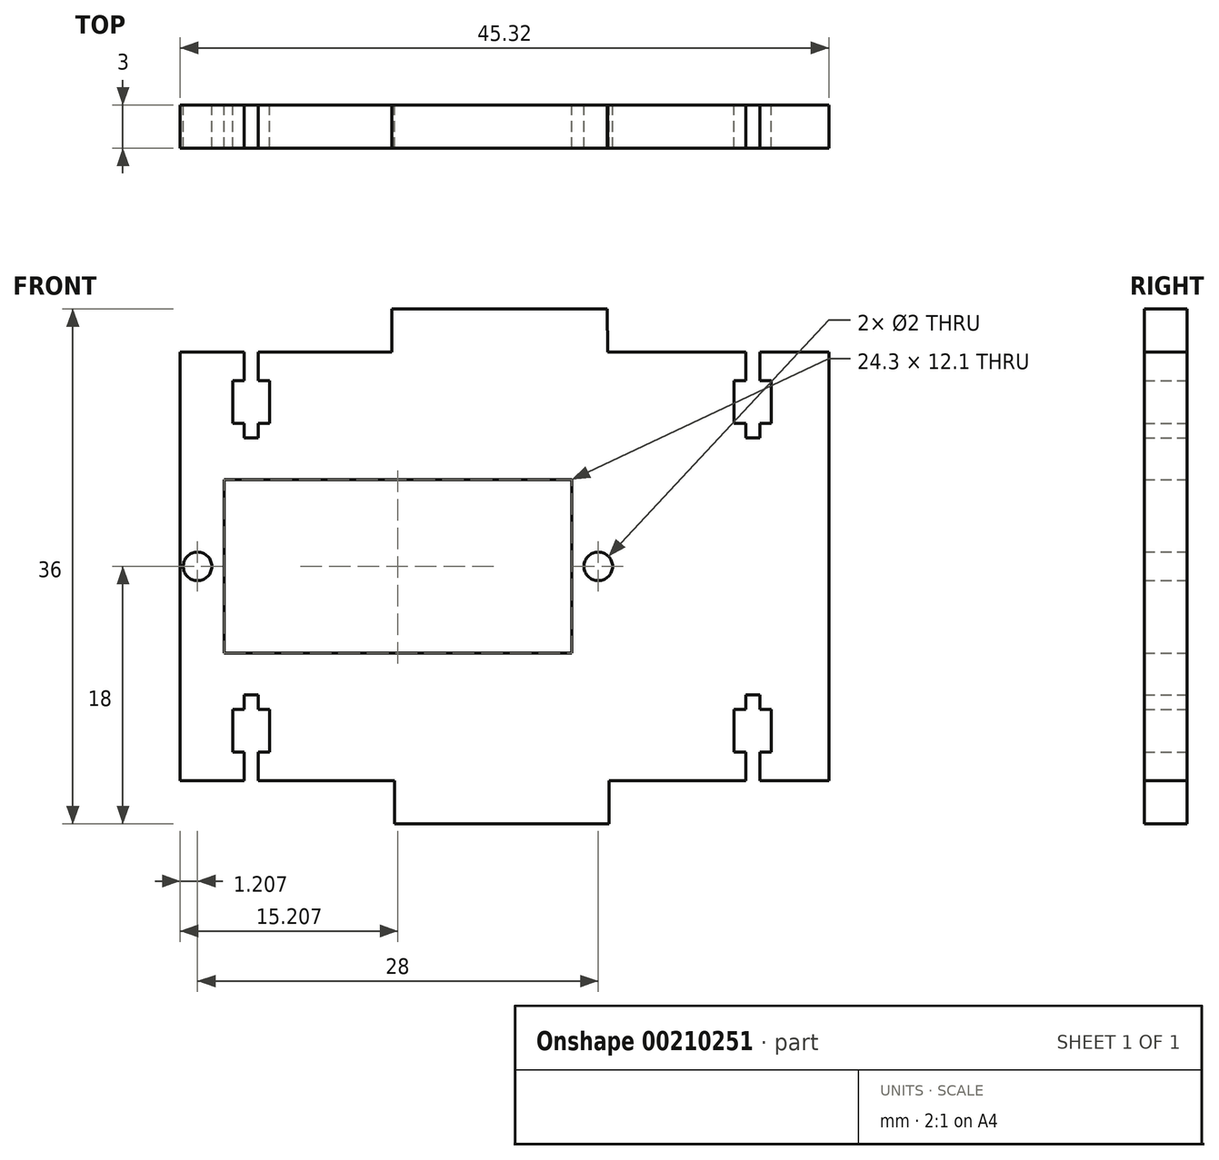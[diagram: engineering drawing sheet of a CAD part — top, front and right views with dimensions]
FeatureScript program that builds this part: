
annotation { "Feature Type Name" : "Feature", "Feature Type Description" : "" }
export const myFeature = defineFeature(function(context is Context, id is Id, definition is map)
    precondition{}
    {
        {
            var Q0;
            Q0=qCreatedBy(makeId("Top.planeOp"),FACE);
            var sketch = newSketch(context, id + "F0", { "sketchPlane" : qUnion([Q0])});
            skCircle(sketch, "E0", {"center": v(38.16, 0) * mm, "radius": 1.5 * mm});
            skArc(sketch, "E1", {"start": v(38.16, -5) * mm, "mid": v(43.16, 0) * mm, "end": v(38.16, 5) * mm});
            skLineSegment(sketch, "E2", {"start": v(38.16, 0) * mm, "end": v(36.66, 0) * mm});
            skLineSegment(sketch, "E3", {"start": v(-21.84, 0) * mm, "end": v(-21.84, 0) * mm});
            skLineSegment(sketch, "E4", {"start": v(-16.84, 5) * mm, "end": v(38.16, 5) * mm});
            skLineSegment(sketch, "E5.MirrorCS", {"start": v(-16.84, -5) * mm, "end": v(38.16, -5) * mm});
            skPoint(sketch, "E6", {"position": v(8.16, 0) * mm});
            skPoint(sketch, "E7", {"position": v(-6.84, 0) * mm});
            skPoint(sketch, "E8", {"position": v(-16.84, 0) * mm});
            skCircle(sketch, "E9", {"center": v(18.16, 0) * mm, "radius": 1.5 * mm});
            skCircle(sketch, "E10", {"center": v(-16.84, 0) * mm, "radius": 1.5 * mm});
            skLineSegment(sketch, "E11", {"start": v(-6.84, 0) * mm, "end": v(-6.84, 1.5) * mm});
            skLineSegment(sketch, "E12", {"start": v(-6.84, 1.5) * mm, "end": v(8.13, 1.5) * mm});
            skLineSegment(sketch, "E13", {"start": v(8.16, 0) * mm, "end": v(8.13, 1.5) * mm});
            skLineSegment(sketch, "E14.MirrorCS", {"start": v(8.16, 0) * mm, "end": v(8.13, -1.5) * mm});
            skLineSegment(sketch, "E15.MirrorCS", {"start": v(-6.84, -1.5) * mm, "end": v(8.13, -1.5) * mm});
            skLineSegment(sketch, "E16.MirrorCS", {"start": v(-6.84, 0) * mm, "end": v(-6.84, -1.5) * mm});
            skPoint(sketch, "E17.visualSharp", {"position": v(-21.84, 5) * mm});
            skArc(sketch, "E17.filletArc", {"start": v(-16.84, 5) * mm, "mid": v(-20.38, 3.54) * mm, "end": v(-21.84, 0) * mm});
            skPoint(sketch, "E18.visualSharp", {"position": v(-21.84, -5) * mm});
            skArc(sketch, "E18.filletArc", {"start": v(-21.84, 0) * mm, "mid": v(-20.38, -3.54) * mm, "end": v(-16.84, -5) * mm});
            skSolve(sketch);
        }
        {
            var Q0;
            Q0=qCreatedBy(makeId("Top.planeOp"),FACE);
            cPlane(context, id + "F1", {"entities" : qUnion([Q0]), "cplaneType" : CPlaneType.OFFSET, "offset" : 30 * mm, "width" : 150 * mm, "height" : 150 * mm});
        }
        {
            var Q0;
            Q0=qCreatedBy(id+"F1.planeOp",FACE);
            var sketch = newSketch(context, id + "F2", { "sketchPlane" : qUnion([Q0])});
            skCircle(sketch, "E19", {"center": v(38.16, 0) * mm, "radius": 2.45 * mm});
            skArc(sketch, "E20", {"start": v(38.16, -5) * mm, "mid": v(43.16, 0) * mm, "end": v(38.16, 5) * mm});
            skLineSegment(sketch, "E21", {"start": v(38.16, 0) * mm, "end": v(35.7, 0) * mm});
            skLineSegment(sketch, "E22", {"start": v(-21.84, 0) * mm, "end": v(-21.84, 0) * mm});
            skLineSegment(sketch, "E23", {"start": v(-16.84, 5) * mm, "end": v(38.16, 5) * mm});
            skLineSegment(sketch, "E24.MirrorCS", {"start": v(-16.84, -5) * mm, "end": v(38.16, -5) * mm});
            skPoint(sketch, "E25", {"position": v(8.16, 0) * mm});
            skPoint(sketch, "E26", {"position": v(-6.84, 0) * mm});
            skPoint(sketch, "E27", {"position": v(-16.84, 0) * mm});
            skCircle(sketch, "E28", {"center": v(18.16, 0) * mm, "radius": 1.5 * mm});
            skCircle(sketch, "E29", {"center": v(-16.84, 0) * mm, "radius": 1.5 * mm});
            skLineSegment(sketch, "E30", {"start": v(-6.84, 0) * mm, "end": v(-6.84, 1.5) * mm});
            skLineSegment(sketch, "E31", {"start": v(-6.84, 1.5) * mm, "end": v(8.13, 1.5) * mm});
            skLineSegment(sketch, "E32", {"start": v(8.16, 0) * mm, "end": v(8.13, 1.5) * mm});
            skLineSegment(sketch, "E33.MirrorCS", {"start": v(8.16, 0) * mm, "end": v(8.13, -1.5) * mm});
            skLineSegment(sketch, "E34.MirrorCS", {"start": v(-6.84, -1.5) * mm, "end": v(8.13, -1.5) * mm});
            skLineSegment(sketch, "E35.MirrorCS", {"start": v(-6.84, 0) * mm, "end": v(-6.84, -1.5) * mm});
            skPoint(sketch, "E36.visualSharp", {"position": v(-21.84, 5) * mm});
            skArc(sketch, "E36.filletArc", {"start": v(-16.84, 5) * mm, "mid": v(-20.38, 3.54) * mm, "end": v(-21.84, 0) * mm});
            skPoint(sketch, "E37.visualSharp", {"position": v(-21.84, -5) * mm});
            skArc(sketch, "E37.filletArc", {"start": v(-21.84, 0) * mm, "mid": v(-20.38, -3.54) * mm, "end": v(-16.84, -5) * mm});
            skSolve(sketch);
        }
        {
            var Q0;
            Q0=qCreatedBy(makeId("Front.planeOp"),FACE);
            var sketch = newSketch(context, id + "F3", { "sketchPlane" : qUnion([Q0])});
            skLineSegment(sketch, "E38", {"start": v(0, 30.19) * mm, "end": v(0, 30) * mm});
            skLineSegment(sketch, "E39.0", {"start": v(36.66, 0) * mm, "end": v(39.66, 0) * mm});
            skLineSegment(sketch, "E39.1", {"start": v(38.16, 0) * mm, "end": v(38.56, 0) * mm});
            skLineSegment(sketch, "E39.2", {"start": v(38.16, 0) * mm, "end": v(36.66, 0) * mm});
            skPoint(sketch, "E39.3", {"position": v(-21.84, 0) * mm});
            skLineSegment(sketch, "E39.4", {"start": v(-16.84, 0) * mm, "end": v(38.16, 0) * mm});
            skLineSegment(sketch, "E39.5", {"start": v(-16.84, 0) * mm, "end": v(-16.84, 0) * mm});
            skPoint(sketch, "E39.6", {"position": v(-21.84, 0) * mm});
            skPoint(sketch, "E39.7", {"position": v(8.16, 0) * mm});
            skPoint(sketch, "E39.8", {"position": v(-6.84, 0) * mm});
            skPoint(sketch, "E39.9", {"position": v(-16.84, 0) * mm});
            skLineSegment(sketch, "E39.10", {"start": v(16.66, 0) * mm, "end": v(19.66, 0) * mm});
            skLineSegment(sketch, "E39.11", {"start": v(-18.34, 0) * mm, "end": v(-17.34, 0) * mm});
            skLineSegment(sketch, "E39.14", {"start": v(8.16, 0) * mm, "end": v(8.13, 0) * mm});
            skLineSegment(sketch, "E39.15", {"start": v(8.16, 0) * mm, "end": v(8.13, 0) * mm});
            skLineSegment(sketch, "E39.16", {"start": v(-6.84, 0) * mm, "end": v(8.13, 0) * mm});
            skPoint(sketch, "E39.18", {"position": v(-21.84, 0) * mm});
            skLineSegment(sketch, "E39.19", {"start": v(-16.84, 0) * mm, "end": v(-21.84, 0) * mm});
            skPoint(sketch, "E39.20", {"position": v(-21.84, 0) * mm});
            skLineSegment(sketch, "E39.21", {"start": v(-21.84, 0) * mm, "end": v(-16.84, 0) * mm});
            skLineSegment(sketch, "E39.22.0", {"start": v(-17.34, 30) * mm, "end": v(-21.84, 30) * mm});
            skLineSegment(sketch, "E39.22.1", {"start": v(-21.84, 30) * mm, "end": v(-16.84, 30) * mm});
            skLineSegment(sketch, "E39.22.2", {"start": v(-16.84, 30) * mm, "end": v(38.16, 30) * mm});
            skLineSegment(sketch, "E39.22.3", {"start": v(38.16, 30) * mm, "end": v(43.16, 30) * mm});
            skLineSegment(sketch, "E39.22.4", {"start": v(38.16, 30) * mm, "end": v(17.7, 30) * mm});
            skLineSegment(sketch, "E40", {"start": v(8.16, 0) * mm, "end": v(8.17, -3) * mm});
            skLineSegment(sketch, "E41", {"start": v(-6.84, 0) * mm, "end": v(-6.83, -3) * mm});
            skLineSegment(sketch, "E42.bottom", {"start": v(-21.84, 30) * mm, "end": v(-7, 30) * mm});
            skLineSegment(sketch, "E42.top", {"start": v(-21.84, 0) * mm, "end": v(43.16, 0) * mm});
            skLineSegment(sketch, "E42.left", {"start": v(-21.84, 30) * mm, "end": v(-21.84, 0) * mm});
            skLineSegment(sketch, "E43.0", {"start": v(-6.83, -3) * mm, "end": v(8.17, -3) * mm});
            skLineSegment(sketch, "E44.0", {"start": v(-17.34, 30) * mm, "end": v(-17.34, 28) * mm});
            skLineSegment(sketch, "E45.0", {"start": v(-16.34, 30) * mm, "end": v(-16.34, 28) * mm});
            skLineSegment(sketch, "E46", {"start": v(-7, 30) * mm, "end": v(-7, 33) * mm});
            skLineSegment(sketch, "E47", {"start": v(8.05, 30) * mm, "end": v(8.04, 33) * mm});
            skLineSegment(sketch, "E48", {"start": v(8.04, 33) * mm, "end": v(-7, 33) * mm});
            skPoint(sketch, "E39.13.end.orphan", {"position": v(8.13, 0) * mm});
            skLineSegment(sketch, "E49.trimOffspring", {"start": v(8.13, 0) * mm, "end": v(38.16, 0) * mm});
            skLineSegment(sketch, "E50.trimOffspring", {"start": v(0, -3) * mm, "end": v(0, -14.95) * mm});
            skLineSegment(sketch, "E51.trimOffspring", {"start": v(0, 30) * mm, "end": v(-16.34, 30) * mm});
            skLineSegment(sketch, "E52.trimOffspring", {"start": v(8.05, 30) * mm, "end": v(43.16, 30) * mm});
            skLineSegment(sketch, "E53.0", {"start": v(-21.8, 25) * mm, "end": v(-21.8, 25) * mm});
            skLineSegment(sketch, "E54.0", {"start": v(-21.8, 28) * mm, "end": v(-21.8, 28) * mm});
            skLineSegment(sketch, "E55.0", {"start": v(-18.14, 28) * mm, "end": v(-18.14, 25) * mm});
            skLineSegment(sketch, "E56.0", {"start": v(-21.8, 30) * mm, "end": v(-21.8, 0) * mm});
            skLineSegment(sketch, "E57.0", {"start": v(-15.54, 28) * mm, "end": v(-15.54, 25) * mm});
            skLineSegment(sketch, "E58.0", {"start": v(-21.8, 24) * mm, "end": v(-21.8, 24) * mm});
            skLineSegment(sketch, "E59.trimOffspring", {"start": v(-16.34, 25) * mm, "end": v(-16.34, 24) * mm});
            skLineSegment(sketch, "E60.trimOffspring", {"start": v(-17.34, 25) * mm, "end": v(-17.34, 24) * mm});
            skLineSegment(sketch, "E61.trimOffspring", {"start": v(-16.34, 25) * mm, "end": v(-15.54, 25) * mm});
            skLineSegment(sketch, "E62.trimOffspring", {"start": v(-17.34, 24) * mm, "end": v(-16.34, 24) * mm});
            skLineSegment(sketch, "E63.trimOffspring", {"start": v(-18.14, 25) * mm, "end": v(-17.34, 25) * mm});
            skLineSegment(sketch, "E64.MirrorCS", {"start": v(-18.14, 5) * mm, "end": v(-17.34, 5) * mm});
            skLineSegment(sketch, "E65.MirrorCS", {"start": v(-16.34, 5) * mm, "end": v(-15.54, 5) * mm});
            skLineSegment(sketch, "E66.MirrorCS", {"start": v(-17.34, 0) * mm, "end": v(-17.34, 2) * mm});
            skLineSegment(sketch, "E67.MirrorCS", {"start": v(-16.34, 5) * mm, "end": v(-16.34, 6) * mm});
            skLineSegment(sketch, "E68.MirrorCS", {"start": v(-18.14, 2) * mm, "end": v(-18.14, 5) * mm});
            skLineSegment(sketch, "E69.MirrorCS", {"start": v(-16.34, 0) * mm, "end": v(-16.34, 2) * mm});
            skLineSegment(sketch, "E70.MirrorCS", {"start": v(-17.34, 5) * mm, "end": v(-17.34, 6) * mm});
            skLineSegment(sketch, "E71.MirrorCS", {"start": v(-15.54, 2) * mm, "end": v(-15.54, 5) * mm});
            skLineSegment(sketch, "E72.MirrorCS", {"start": v(-17.34, 6) * mm, "end": v(-16.34, 6) * mm});
            skLineSegment(sketch, "E73", {"start": v(-18.14, 28) * mm, "end": v(-17.34, 28) * mm});
            skLineSegment(sketch, "E74", {"start": v(-16.34, 28) * mm, "end": v(-15.54, 28) * mm});
            skLineSegment(sketch, "E75", {"start": v(-16.34, 2) * mm, "end": v(-15.54, 2) * mm});
            skLineSegment(sketch, "E76", {"start": v(-18.14, 2) * mm, "end": v(-17.34, 2) * mm});
            skLineSegment(sketch, "E77.trimOffspring", {"start": v(-16.84, 0) * mm, "end": v(-15.34, 0) * mm});
            skLineSegment(sketch, "E78.trimOffspring", {"start": v(-16.34, 0) * mm, "end": v(-6.84, 0) * mm});
            skPoint(sketch, "E79.orphan", {"position": v(-16.84, 30) * mm});
            skPoint(sketch, "E80.end.orphan", {"position": v(38.56, 0) * mm});
            skPoint(sketch, "E81", {"position": v(-17.34, 30) * mm});
            skPoint(sketch, "E82", {"position": v(-16.34, 30) * mm});
            skLineSegment(sketch, "E83.0", {"start": v(17.7, 30) * mm, "end": v(17.7, 27.99) * mm});
            skLineSegment(sketch, "E84.0", {"start": v(18.7, 30) * mm, "end": v(18.7, 27.99) * mm});
            skLineSegment(sketch, "E85.0", {"start": v(16.9, 27.99) * mm, "end": v(16.9, 24.99) * mm});
            skLineSegment(sketch, "E86.0", {"start": v(19.5, 27.99) * mm, "end": v(19.5, 24.99) * mm});
            skLineSegment(sketch, "E87.trimOffspring", {"start": v(18.7, 24.99) * mm, "end": v(18.7, 23.99) * mm});
            skLineSegment(sketch, "E88.trimOffspring", {"start": v(17.7, 24.99) * mm, "end": v(17.7, 23.99) * mm});
            skLineSegment(sketch, "E89.trimOffspring", {"start": v(18.7, 24.99) * mm, "end": v(19.5, 24.99) * mm});
            skLineSegment(sketch, "E90.trimOffspring", {"start": v(17.7, 23.99) * mm, "end": v(18.7, 23.99) * mm});
            skLineSegment(sketch, "E91.trimOffspring", {"start": v(16.9, 24.99) * mm, "end": v(17.7, 24.99) * mm});
            skLineSegment(sketch, "E92", {"start": v(16.9, 27.99) * mm, "end": v(17.7, 27.99) * mm});
            skLineSegment(sketch, "E93", {"start": v(18.7, 27.99) * mm, "end": v(19.5, 27.99) * mm});
            skLineSegment(sketch, "E94", {"start": v(-21.8, 15) * mm, "end": v(-21.6, 15) * mm});
            skPoint(sketch, "E95.MirrorP", {"position": v(18.7, 0.01) * mm});
            skLineSegment(sketch, "E96.MirrorCS", {"start": v(16.9, 2.01) * mm, "end": v(16.9, 5.01) * mm});
            skLineSegment(sketch, "E97.MirrorCS", {"start": v(18.7, 5.01) * mm, "end": v(19.5, 5.01) * mm});
            skPoint(sketch, "E98.MirrorP", {"position": v(17.7, 0.01) * mm});
            skLineSegment(sketch, "E99.MirrorCS", {"start": v(16.9, 2.01) * mm, "end": v(17.7, 2.01) * mm});
            skLineSegment(sketch, "E100.MirrorCS", {"start": v(18.7, 5.01) * mm, "end": v(18.7, 6.01) * mm});
            skLineSegment(sketch, "E101.MirrorCS", {"start": v(19.5, 2.01) * mm, "end": v(19.5, 5.01) * mm});
            skLineSegment(sketch, "E102.MirrorCS", {"start": v(18.7, 2.01) * mm, "end": v(19.5, 2.01) * mm});
            skLineSegment(sketch, "E103.MirrorCS", {"start": v(17.7, 5.01) * mm, "end": v(17.7, 6.01) * mm});
            skLineSegment(sketch, "E104.MirrorCS", {"start": v(16.9, 5.01) * mm, "end": v(17.7, 5.01) * mm});
            skLineSegment(sketch, "E105.MirrorCS", {"start": v(17.7, 0) * mm, "end": v(17.7, 2.01) * mm});
            skLineSegment(sketch, "E106.MirrorCS", {"start": v(18.7, 0) * mm, "end": v(18.7, 2.01) * mm});
            skLineSegment(sketch, "E107.MirrorCS", {"start": v(17.7, 6.01) * mm, "end": v(18.7, 6.01) * mm});
            skLineSegment(sketch, "E108.0", {"start": v(-18.74, 8.95) * mm, "end": v(5.56, 8.95) * mm});
            skLineSegment(sketch, "E109.0", {"start": v(-18.74, 21.05) * mm, "end": v(5.56, 21.05) * mm});
            skLineSegment(sketch, "E110.0", {"start": v(5.56, 21.05) * mm, "end": v(5.56, 8.95) * mm});
            skLineSegment(sketch, "E111.trimOffspring", {"start": v(-18.74, 21.05) * mm, "end": v(-18.74, 8.95) * mm});
            skPoint(sketch, "E112", {"position": v(-6.6, 15) * mm});
            skCircle(sketch, "E113", {"center": v(-20.6, 15) * mm, "radius": 1 * mm});
            skCircle(sketch, "E114.MirrorC", {"center": v(7.4, 15) * mm, "radius": 1 * mm});
            skLineSegment(sketch, "E115.trimOffspring", {"start": v(39.66, 0) * mm, "end": v(43.16, 0) * mm});
            skLineSegment(sketch, "E116", {"start": v(23.52, 30) * mm, "end": v(23.52, 0) * mm});
            skSolve(sketch);
        }
        {
            var Q0;
            {var subQ19=sQuery(id+"F3.wireOp",EDGE,"E39.22.2");Q0=makeQuery(id+"F3.imprint","IMPRINT",FACE,{"disambiguationData":[TD([[makeQuery(id+"F3.imprint","IMPRINT",EDGE,{"derivedFrom":subQ19}),-1.0]])]});}
            var Q1;
            {var subQ1=sQuery(id+"F3.wireOp",EDGE,"E39.22.2");Q1=makeQuery(id+"F3.imprint","IMPRINT",FACE,{"disambiguationData":[TD([[makeQuery(id+"F3.imprint","IMPRINT",EDGE,{"derivedFrom":subQ1}),1.0]])]});}
            var Q2;
            {var subQ6=sQuery(id+"F3.wireOp",EDGE,"E40");Q2=makeQuery(id+"F3.imprint","IMPRINT",FACE,{"disambiguationData":[TD([[makeQuery(id+"F3.imprint","IMPRINT",EDGE,{"derivedFrom":subQ6}),-1.0]])]});}
            extrude(context, id + "F4", {"entities" : qUnion([Q0, Q1, Q2]), "depth" : 3 * mm});
        }
    });
